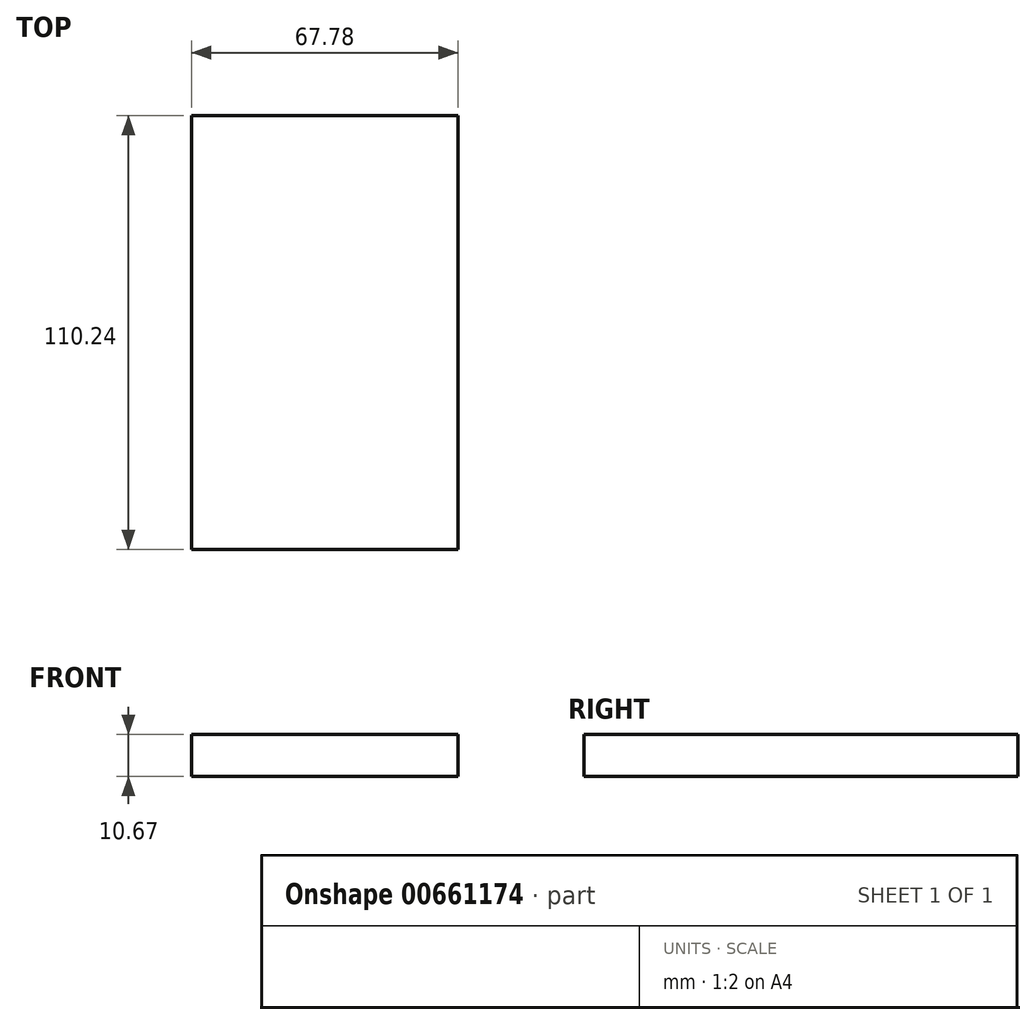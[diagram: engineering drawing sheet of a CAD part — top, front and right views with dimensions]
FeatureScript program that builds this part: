
annotation { "Feature Type Name" : "Feature", "Feature Type Description" : "" }
export const myFeature = defineFeature(function(context is Context, id is Id, definition is map)
    precondition{}
    {
        {
            var Q0;
            Q0=qCreatedBy(makeId("Top.planeOp"),FACE);
            var sketch = newSketch(context, id + "F0", { "sketchPlane" : qUnion([Q0])});
            skLineSegment(sketch, "E0.bottom", {"start": v(33.89, 55.12) * mm, "end": v(-33.89, 55.12) * mm});
            skLineSegment(sketch, "E0.top", {"start": v(33.89, -55.12) * mm, "end": v(-33.89, -55.12) * mm});
            skLineSegment(sketch, "E0.left", {"start": v(33.89, 55.12) * mm, "end": v(33.89, -55.12) * mm});
            skLineSegment(sketch, "E0.right", {"start": v(-33.89, 55.12) * mm, "end": v(-33.89, -55.12) * mm});
            skPoint(sketch, "E0.middle", {"position": v(0, 0) * mm});
            skSolve(sketch);
        }
        {
            var Q0;
            Q0=qSketchRegion(id+"F0",true);
            extrude(context, id + "F1", {"entities" : qUnion([Q0]), "depth" : 10.67 * mm, "offsetDistance" : 25.4 * mm});
        }
    });
